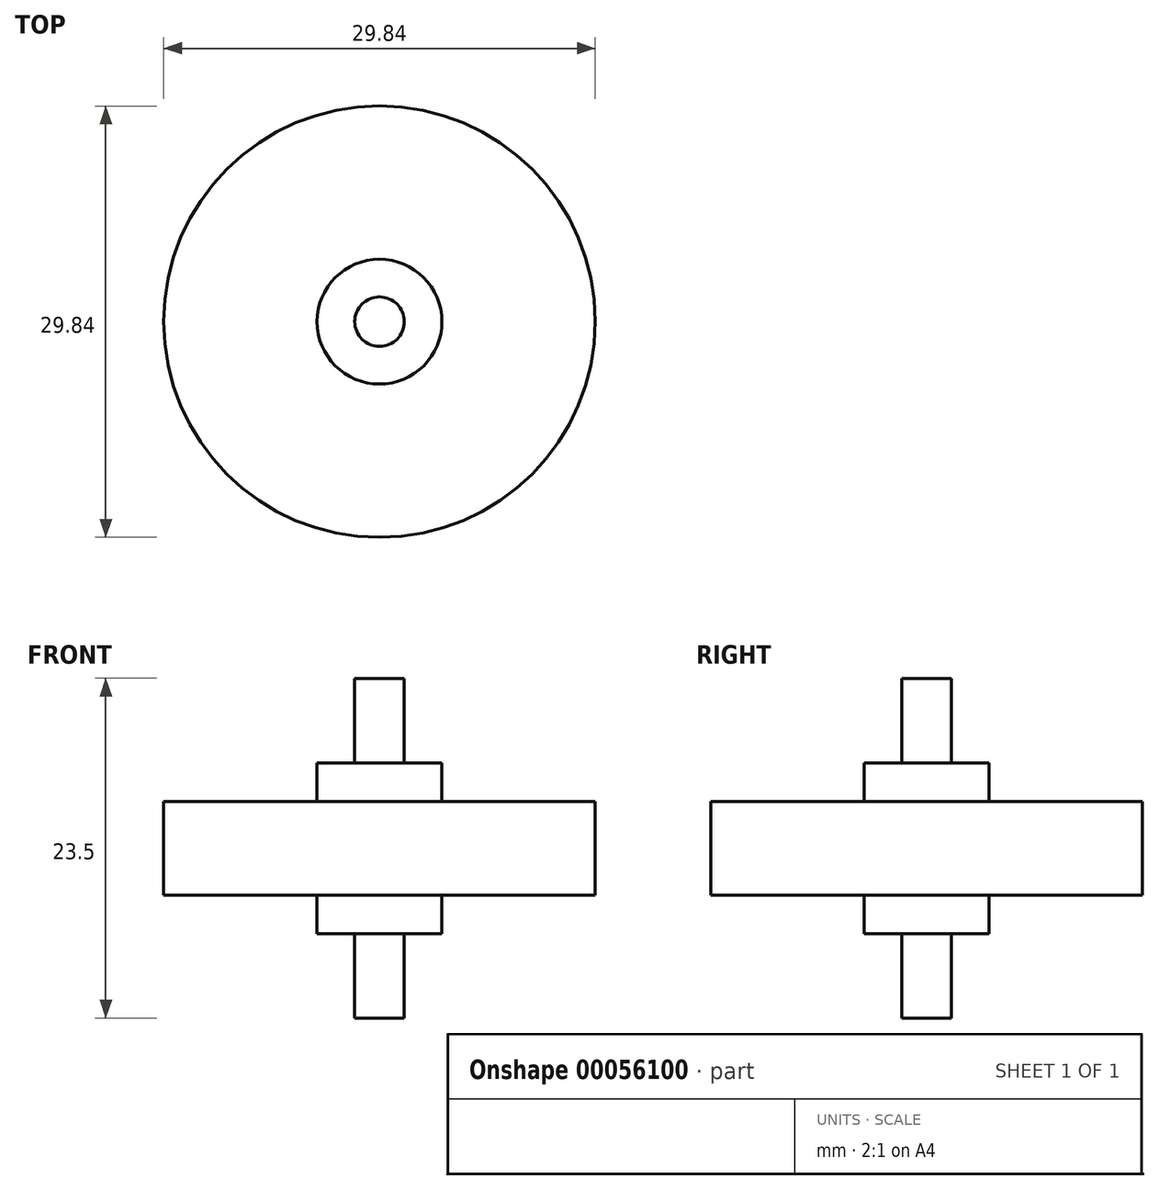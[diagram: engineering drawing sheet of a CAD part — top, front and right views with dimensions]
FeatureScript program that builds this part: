
annotation { "Feature Type Name" : "Feature", "Feature Type Description" : "" }
export const myFeature = defineFeature(function(context is Context, id is Id, definition is map)
    precondition{}
    {
        {
            var Q0;
            Q0=qCreatedBy(makeId("Top.planeOp"),FACE);
            var sketch = newSketch(context, id + "F0", { "sketchPlane" : qUnion([Q0])});
            skCircle(sketch, "E0", {"center": v(0, 0) * mm, "radius": 14.92 * mm});
            skLineSegment(sketch, "E1", {"start": v(0, 0) * mm, "end": v(14.86, 1.34) * mm});
            skSolve(sketch);
        }
        {
            var Q0;
            Q0 = qSketchRegion(id + "F0", true);
            extrude(context, id + "F1", {"entities" : qUnion([Q0]), "endBound" : BoundingType.SYMMETRIC, "depth" : 6.48 * mm});
        }
        {
            var Q0;
            Q0=qCreatedBy(makeId("Top.planeOp"),FACE);
            var sketch = newSketch(context, id + "F2", { "sketchPlane" : qUnion([Q0])});
            skCircle(sketch, "E2", {"center": v(0, 0) * mm, "radius": 4.32 * mm});
            skLineSegment(sketch, "E3", {"start": v(0, 0) * mm, "end": v(4.31, 0.24) * mm});
            skSolve(sketch);
        }
        {
            var Q0;
            Q0 = qSketchRegion(id + "F2", true);
            extrude(context, id + "F3", {"entities" : qUnion([Q0]), "operationType" : NewBodyOperationType.ADD, "endBound" : BoundingType.SYMMETRIC, "depth" : 11.8 * mm});
        }
        {
            var Q0;
            Q0=qCreatedBy(makeId("Top.planeOp"),FACE);
            var sketch = newSketch(context, id + "F4", { "sketchPlane" : qUnion([Q0])});
            skCircle(sketch, "E4", {"center": v(0, 0) * mm, "radius": 1.71 * mm});
            skLineSegment(sketch, "E5", {"start": v(0, 0) * mm, "end": v(1.71, 0) * mm});
            skSolve(sketch);
        }
        {
            var Q0;
            Q0 = qSketchRegion(id + "F4", true);
            extrude(context, id + "F5", {"entities" : qUnion([Q0]), "operationType" : NewBodyOperationType.ADD, "endBound" : BoundingType.SYMMETRIC, "depth" : 23.5 * mm});
        }
    });
